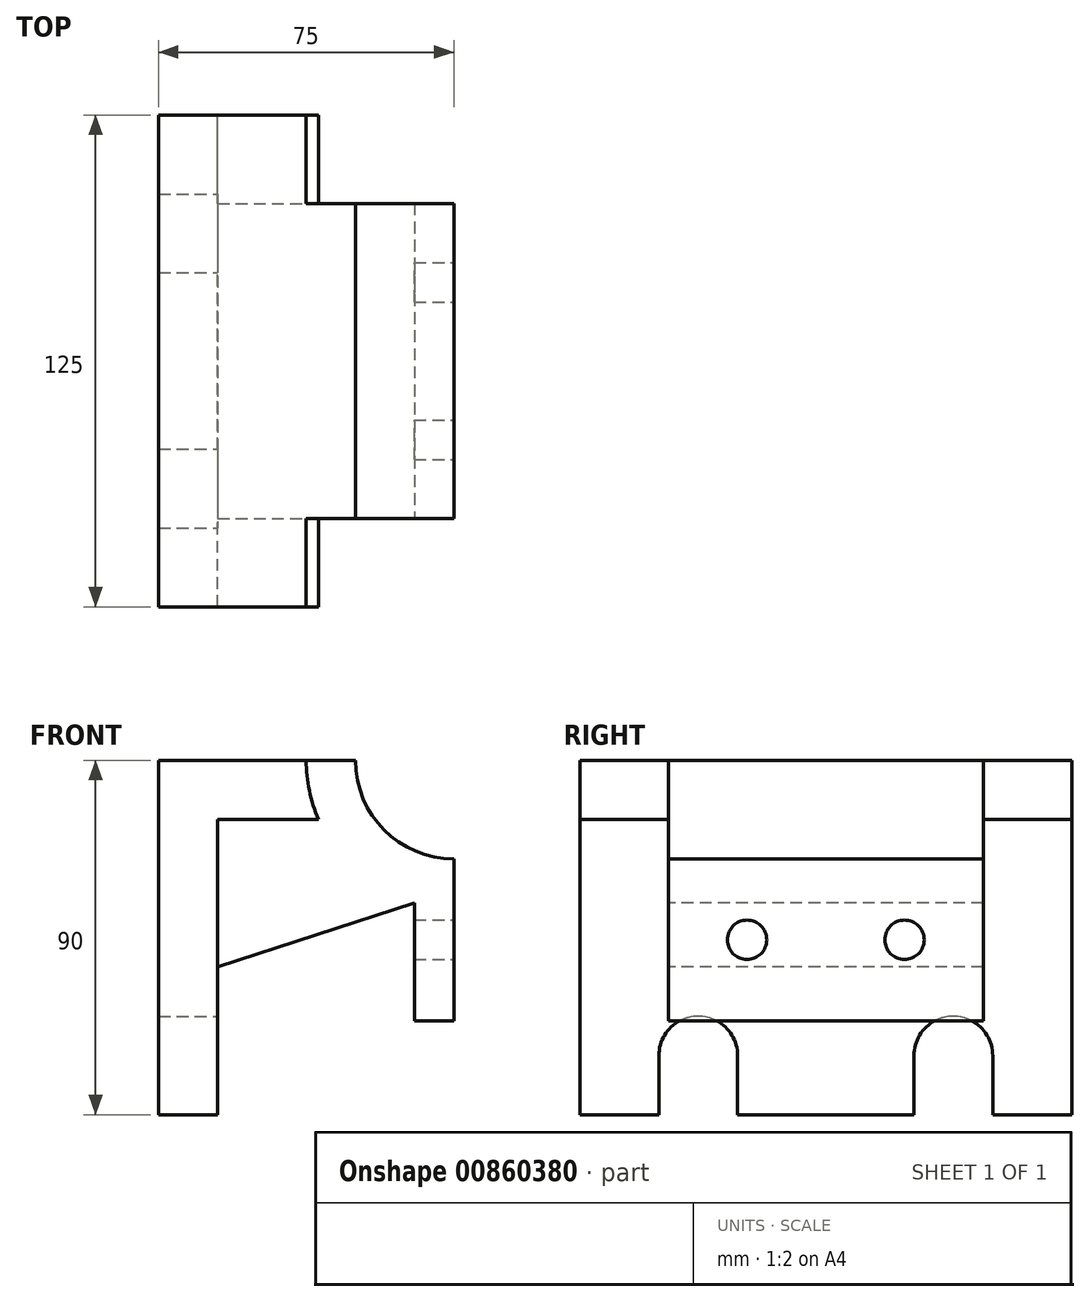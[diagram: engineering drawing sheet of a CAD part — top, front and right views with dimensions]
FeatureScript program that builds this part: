
annotation { "Feature Type Name" : "Feature", "Feature Type Description" : "" }
export const myFeature = defineFeature(function(context is Context, id is Id, definition is map)
    precondition{}
    {
        {
            var Q0;
            Q0=qCreatedBy(makeId("Front.planeOp"),FACE);
            var sketch = newSketch(context, id + "F0", { "sketchPlane" : qUnion([Q0])});
            skLineSegment(sketch, "E0", {"start": v(-75, 0) * mm, "end": v(-75, -90) * mm});
            skLineSegment(sketch, "E1", {"start": v(-75, -90) * mm, "end": v(-60, -90) * mm});
            skLineSegment(sketch, "E2", {"start": v(-60, -90) * mm, "end": v(-60, -15) * mm});
            skLineSegment(sketch, "E3", {"start": v(60, -15) * mm, "end": v(60, 0) * mm});
            skLineSegment(sketch, "E4", {"start": v(-60, -15) * mm, "end": v(-75, -15) * mm});
            skLineSegment(sketch, "E5", {"start": v(-75, 0) * mm, "end": v(0, 0) * mm});
            skLineSegment(sketch, "E6", {"start": v(0, 0) * mm, "end": v(60, 0) * mm});
            skCircle(sketch, "E7", {"center": v(0, 0) * mm, "radius": 25 * mm});
            skCircle(sketch, "E8", {"center": v(0, 0) * mm, "radius": 37.5 * mm});
            skLineSegment(sketch, "E9", {"start": v(-60, -15) * mm, "end": v(60, -15) * mm});
            skLineSegment(sketch, "E10", {"start": v(-60, -52.5) * mm, "end": v(-10, -36.14) * mm});
            skLineSegment(sketch, "E11", {"start": v(0, -25) * mm, "end": v(0, -66.14) * mm});
            skLineSegment(sketch, "E12", {"start": v(0, -66.14) * mm, "end": v(-10, -66.14) * mm});
            skLineSegment(sketch, "E13", {"start": v(-10, -66.14) * mm, "end": v(-10, -36.14) * mm});
            skPoint(sketch, "E14", {"position": v(0, -37.5) * mm});
            skSolve(sketch);
        }
        {
            var Q0;
            {var subQ3=sQuery(id+"F0.wireOp",EDGE,"E1");Q0=makeQuery(id+"F0.imprint","IMPRINT",FACE,{"disambiguationData":[TD([[makeQuery(id+"F0.imprint","IMPRINT",EDGE,{"derivedFrom":subQ3}),1.0]])]});}
            var Q1;
            {var subQ7=sQuery(id+"F0.wireOp",EDGE,"E4");Q1=makeQuery(id+"F0.imprint","IMPRINT",FACE,{"disambiguationData":[TD([[makeQuery(id+"F0.imprint","IMPRINT",EDGE,{"derivedFrom":subQ7}),-1.0]])]});}
            extrude(context, id + "F1", {"entities" : qUnion([Q0, Q1]), "endBound" : BoundingType.SYMMETRIC, "depth" : 125 * mm, "offsetDistance" : 25 * mm});
        }
        {
            var Q0;
            Q0=makeQuery(id+"F1.opExtrude","SWEPT_FACE",FACE,{"disambiguationData":[OSD([sQuery(id+"F0.wireOp",EDGE,"E2")])]});
            var sketch = newSketch(context, id + "F2", { "sketchPlane" : qUnion([Q0])});
            skPoint(sketch, "E15.firstSnap0", {"position": v(40, -33.75) * mm});
            skLineSegment(sketch, "E16.left", {"start": v(62.5, -90) * mm, "end": v(62.5, -52.5) * mm, "construction": true});
            skLineSegment(sketch, "E16.right", {"start": v(-62.5, -90) * mm, "end": v(-62.5, -52.5) * mm, "construction": true});
            skLineSegment(sketch, "E17", {"start": v(62.5, -52.5) * mm, "end": v(42.4, -52.5) * mm, "construction": true});
            skLineSegment(sketch, "E18", {"start": v(-62.5, -52.5) * mm, "end": v(-42.4, -52.5) * mm, "construction": true});
            skLineSegment(sketch, "E19", {"start": v(42.4, -52.5) * mm, "end": v(42.4, -62.5) * mm, "construction": true});
            skLineSegment(sketch, "E20", {"start": v(42.4, -62.5) * mm, "end": v(-42.4, -62.5) * mm, "construction": true});
            skLineSegment(sketch, "E21", {"start": v(-42.4, -62.5) * mm, "end": v(-42.4, -52.5) * mm, "construction": true});
            skLineSegment(sketch, "E22.bottom", {"start": v(42.4, -75) * mm, "end": v(22.4, -75) * mm});
            skLineSegment(sketch, "E22.top", {"start": v(42.4, -90) * mm, "end": v(22.4, -90) * mm});
            skLineSegment(sketch, "E22.left", {"start": v(42.4, -75) * mm, "end": v(42.4, -90) * mm});
            skLineSegment(sketch, "E22.right", {"start": v(22.4, -75) * mm, "end": v(22.4, -90) * mm});
            skArc(sketch, "E23", {"start": v(42.4, -75) * mm, "mid": v(32.4, -65) * mm, "end": v(22.4, -75) * mm});
            skLineSegment(sketch, "E24", {"start": v(0, -52.5) * mm, "end": v(0, -90) * mm, "construction": true});
            skLineSegment(sketch, "E25.MirrorCS", {"start": v(-22.4, -75) * mm, "end": v(-22.4, -90) * mm});
            skLineSegment(sketch, "E26.MirrorCS", {"start": v(-42.4, -75) * mm, "end": v(-22.4, -75) * mm});
            skLineSegment(sketch, "E27.MirrorCS", {"start": v(-42.4, -75) * mm, "end": v(-42.4, -90) * mm});
            skLineSegment(sketch, "E28.MirrorCS", {"start": v(-42.4, -90) * mm, "end": v(-22.4, -90) * mm});
            skArc(sketch, "E29.MirrorCS", {"start": v(-42.4, -75) * mm, "mid": v(-32.4, -65) * mm, "end": v(-22.4, -75) * mm});
            skSolve(sketch);
        }
        {
            var Q0;
            Q0=qSketchRegion(id+"F2",true);
            extrude(context, id + "F3", {"entities" : qUnion([Q0]), "operationType" : NewBodyOperationType.REMOVE, "endBound" : BoundingType.THROUGH_ALL, "oppositeDirection" : true, "depth" : 25 * mm, "offsetDistance" : 25 * mm});
        }
        {
            var Q0;
            {var subQ3=sQuery(id+"F0.wireOp",EDGE,"E10");Q0=makeQuery(id+"F0.imprint","IMPRINT",FACE,{"disambiguationData":[TD([[makeQuery(id+"F0.imprint","IMPRINT",EDGE,{"derivedFrom":subQ3}),1.0]])]});}
            var Q1;
            {var subQ2=sQuery(id+"F0.wireOp",EDGE,"E11");var subQ5=sQuery(id+"F0.wireOp",EDGE,"E7");var subQ8=makeQuery(id+"F0.imprint","INTERSECT",VERTEX,{"derivedFrom":[subQ5,subQ2]});Q1=makeQuery(id+"F0.imprint","IMPRINT",FACE,{"disambiguationData":[TD([[makeQuery(id+"F0.imprint","IMPRINT",EDGE,{"disambiguationData":[TD([[subQ8,1.0]])],"derivedFrom":subQ5}),-1.0]])]});}
            var Q2;
            {var subQ4=sQuery(id+"F0.wireOp",EDGE,"E12");Q2=makeQuery(id+"F0.imprint","IMPRINT",FACE,{"disambiguationData":[TD([[makeQuery(id+"F0.imprint","IMPRINT",EDGE,{"derivedFrom":subQ4}),-1.0]])]});}
            var Q3;
            {var subQ0=sQuery(id+"F0.wireOp",EDGE,"E8");var subQ1=sQuery(id+"F0.wireOp",EDGE,"E5");var subQ2=makeQuery(id+"F0.imprint","INTERSECT",VERTEX,{"derivedFrom":[subQ1,subQ0]});Q3=makeQuery(id+"F0.imprint","IMPRINT",FACE,{"disambiguationData":[TD([[makeQuery(id+"F0.imprint","IMPRINT",EDGE,{"disambiguationData":[TD([[subQ2,-1.0]])],"derivedFrom":subQ1}),-1.0]])]});}
            extrude(context, id + "F4", {"entities" : qUnion([Q0, Q1, Q2, Q3]), "operationType" : NewBodyOperationType.ADD, "endBound" : BoundingType.SYMMETRIC, "oppositeDirection" : true, "depth" : 80 * mm, "offsetDistance" : 25 * mm});
        }
        {
            var Q0;
            Q0=makeQuery(id+"F4.opExtrude","SWEPT_FACE",FACE,{"disambiguationData":[OSD([sQuery(id+"F0.wireOp",EDGE,"E11")])]});
            var sketch = newSketch(context, id + "F5", { "sketchPlane" : qUnion([Q0])});
            skLineSegment(sketch, "E30.bottom", {"start": v(-40, -66.14) * mm, "end": v(40, -66.14) * mm, "construction": true});
            skLineSegment(sketch, "E30.top", {"start": v(-40, -25) * mm, "end": v(40, -25) * mm, "construction": true});
            skLineSegment(sketch, "E30.left", {"start": v(-40, -66.14) * mm, "end": v(-40, -25) * mm, "construction": true});
            skLineSegment(sketch, "E30.right", {"start": v(40, -66.14) * mm, "end": v(40, -25) * mm, "construction": true});
            skLineSegment(sketch, "E31", {"start": v(0, -66.14) * mm, "end": v(0, -25) * mm, "construction": true});
            skLineSegment(sketch, "E32", {"start": v(0, -25) * mm, "end": v(-40, -66.14) * mm, "construction": true});
            skLineSegment(sketch, "E33", {"start": v(-40, -25) * mm, "end": v(0, -66.14) * mm, "construction": true});
            skLineSegment(sketch, "E34", {"start": v(40, -25) * mm, "end": v(0, -66.14) * mm, "construction": true});
            skLineSegment(sketch, "E35", {"start": v(40, -66.14) * mm, "end": v(0, -25) * mm, "construction": true});
            skCircle(sketch, "E36", {"center": v(-20, -45.57) * mm, "radius": 5 * mm});
            skCircle(sketch, "E37", {"center": v(20, -45.57) * mm, "radius": 5 * mm});
            skSolve(sketch);
        }
        {
            var Q0;
            Q0=makeQuery(id+"F5.imprint","IMPRINT",FACE,{"disambiguationData":[TD([[makeQuery(id+"F5.imprint","IMPRINT",EDGE,{"derivedFrom":sQuery(id+"F5.wireOp",EDGE,"E36")}),1.0]])]});
            var Q1;
            Q1=makeQuery(id+"F5.imprint","IMPRINT",FACE,{"disambiguationData":[TD([[makeQuery(id+"F5.imprint","IMPRINT",EDGE,{"derivedFrom":sQuery(id+"F5.wireOp",EDGE,"E37")}),1.0]])]});
            extrude(context, id + "F6", {"entities" : qUnion([Q0, Q1]), "operationType" : NewBodyOperationType.REMOVE, "oppositeDirection" : true, "depth" : 15 * mm, "offsetDistance" : 25 * mm});
        }
    });
